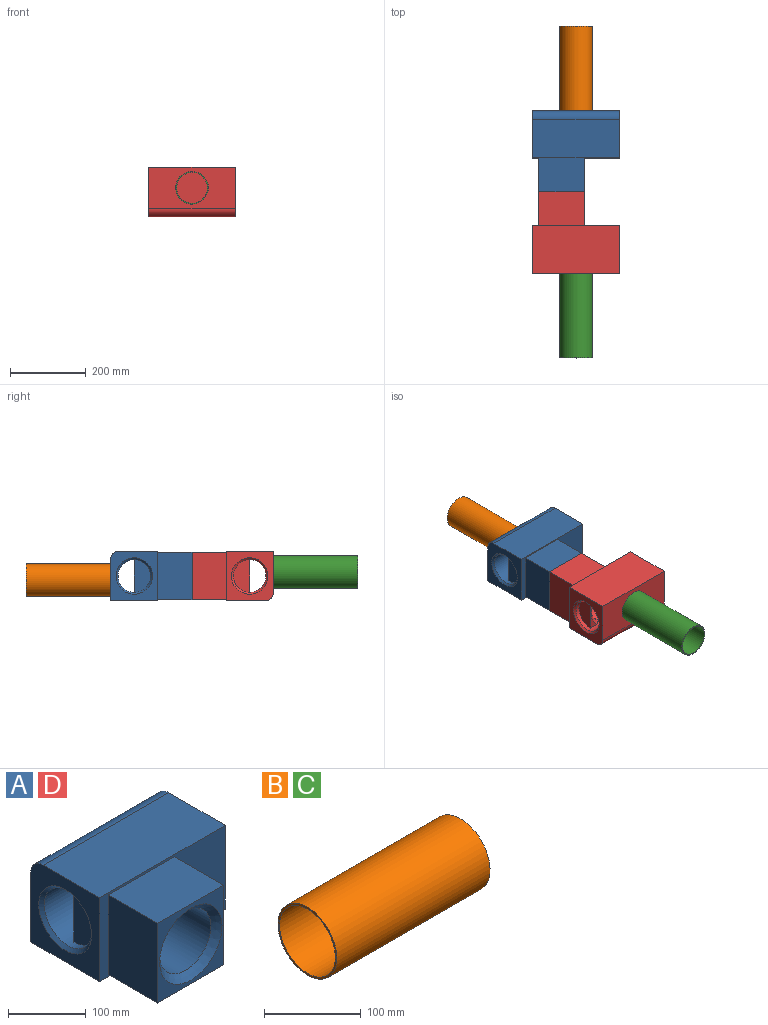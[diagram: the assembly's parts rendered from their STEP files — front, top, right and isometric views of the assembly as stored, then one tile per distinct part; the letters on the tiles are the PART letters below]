
ASSEMBLY  parts=4 mates=2
PART A: 25 faces, bbox 228.6x214.9x132 mm
  f0: plane 120.25x89.91mm, normal (0,0,-1), area 10812.2mm2, adj f3,f4,f5,f9
  f1: plane 120.25x89.91mm, normal (0,0,1), area 10812.2mm2, adj f3,f4,f5,f9
  f2: cylinder r=46.53mm len=93.05mm, axis (0,1,0), area 23315.2mm2, adj f16,f22
  f3: plane 125.38x89.91mm, normal (1,0,0), area 11273.7mm2, adj f0,f1,f5,f9
  f4: plane 125.38x89.91mm, normal (-1,0,0), area 11273.7mm2, adj f0,f1,f5,f9
  f5: plane 125.38x120.25mm, normal (0,-1,0), area 4982.1mm2, adj f0,f1,f3,f4,f22
  f6: plane 132x124.97mm, normal (-1,0,0), area 9127.2mm2, adj f8,f9,f10,f11,f20,f21
  f7: plane 132x124.97mm, normal (1,0,0), area 10582.2mm2, adj f8,f9,f10,f11,f12,f20
  f8: plane 228.6x124.97mm, normal (0,0,-1), area 28568.5mm2, adj f6,f7,f9,f11
  f9: plane 228.6x132mm, normal (0,-1,0), area 15097.3mm2, adj f0,f1,f3,f4,f6,f7,f8,f10
  f10: plane 228.6x102.75mm, normal (0,0,1), area 23487.9mm2, adj f6,f7,f9,f20
  f11: plane 228.6x109.77mm, normal (0,1,0), area 25094mm2, adj f6,f7,f8,f20
  f12: cylinder r=43mm len=223.52mm, axis (-1,0,0), area 53682.6mm2, adj f7,f13,f14,f15,f17,f18,f19,f21
  f13: plane 85.99x23.18mm, normal (0,1,0), area 815.2mm2, adj f12,f15,f24
  f14: cylinder r=46.53mm len=83.56mm, axis (0,1,0), area 2325.8mm2, adj f12,f24
  f15: plane 85.99x43mm, normal (1,0,0), area 2903.9mm2, adj f12,f13
  f16: plane 93.05x93.05mm, normal (0,-1,0), area 6800.9mm2, adj f2
  f17: plane 85.99x23.18mm, normal (0,1,0), area 815.2mm2, adj f12,f18,f23
  f18: plane 85.99x43mm, normal (-1,0,0), area 2903.9mm2, adj f12,f17
  f19: cylinder r=46.53mm len=83.56mm, axis (0,1,0), area 2325.8mm2, adj f12,f23
  f20: cylinder r=22.23mm len=228.6mm, axis (1,0,0), area 7980.6mm2, adj f6,f7,f10,f11
  f21: cone r=48.08mm half-angle=45deg, axis (-1,0,0), area 2057.7mm2, adj f6,f12
  f22: cone r=46.53mm half-angle=45deg, axis (0,-1,0), area 4659.1mm2, adj f2,f5
  f23: cone r=56.69mm half-angle=45deg, axis (0,1,0), area 1445.4mm2, adj f12,f17,f19
  f24: cone r=56.69mm half-angle=45deg, axis (0,1,0), area 1445.4mm2, adj f12,f13,f14
PART B: 4 faces, bbox 223.5x86x86 mm
  f0: cylinder r=40.68mm len=223.52mm, axis (-1,0,0), area 57134.4mm2, adj f2,f3
  f1: cylinder r=43mm len=223.52mm, axis (-1,0,0), area 60384.6mm2, adj f2,f3
  f2: plane 85.99x85.99mm, normal (1,0,0), area 608.4mm2, adj f0,f1
  f3: plane 85.99x85.99mm, normal (-1,0,0), area 608.4mm2, adj f0,f1
PART C: same geometry as B
PART D: same geometry as A
PLACE A t=(-111.85,-123.22,217.19)mm
PLACE B rot(axis=(0.58,-0.58,-0.58),120deg) t=(-73.75,244.07,206.08)mm
PLACE C rot(axis=(0.58,0.58,0.58),120deg) t=(-73.75,-795.3,228.31)mm
PLACE D rot(axis=(1,0,0),180deg) t=(-111.85,-428.02,217.19)mm
MATE fastened B.f1 <-> A.f11  axis (0,1,0) through (-73.75,-60.73,206.08)mm
MATE fastened D.f11 <-> C.f1  axis (0,-1,0) through (-73.75,-490.5,228.31)mm
